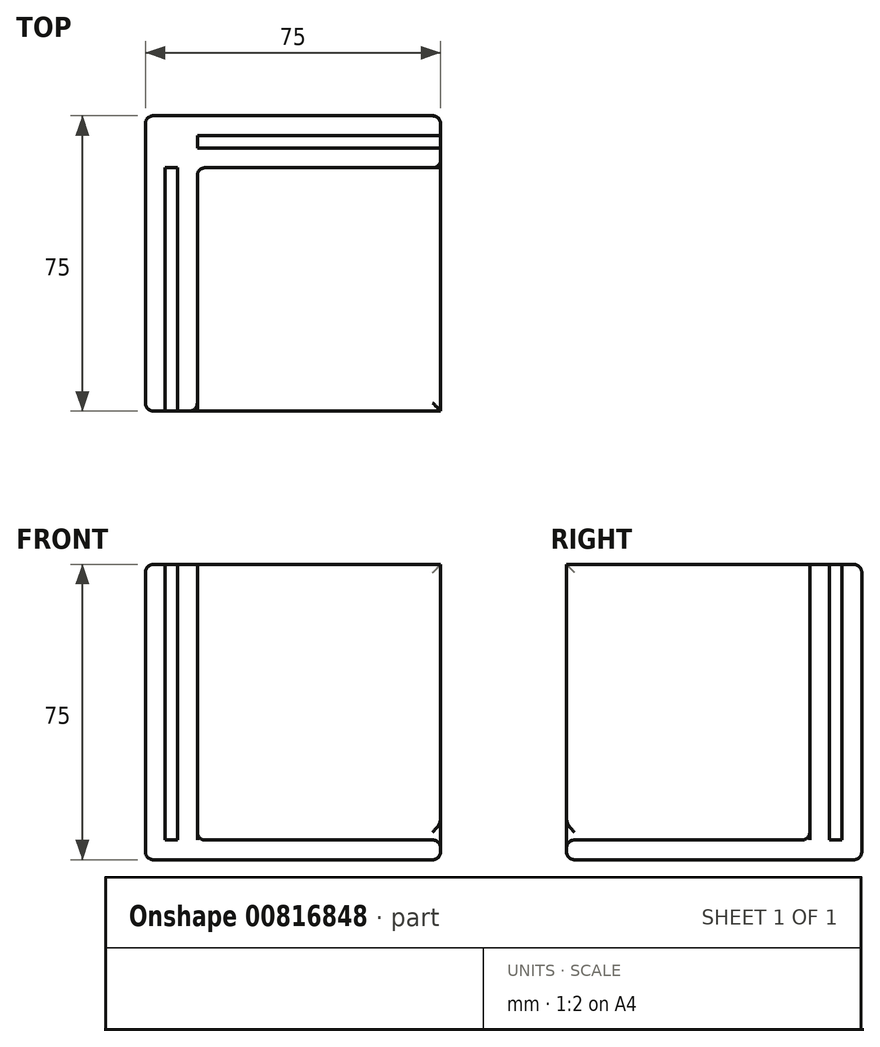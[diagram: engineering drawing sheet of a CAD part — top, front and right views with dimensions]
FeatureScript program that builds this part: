
annotation { "Feature Type Name" : "Feature", "Feature Type Description" : "" }
export const myFeature = defineFeature(function(context is Context, id is Id, definition is map)
    precondition{}
    {
        {
            var Q0;
            Q0=qCreatedBy(makeId("Top.planeOp"),FACE);
            var sketch = newSketch(context, id + "F0", { "sketchPlane" : qUnion([Q0])});
            skLineSegment(sketch, "E0.bottom", {"start": v(37.5, -37.5) * mm, "end": v(-37.5, -37.5) * mm});
            skLineSegment(sketch, "E0.top", {"start": v(37.5, 37.5) * mm, "end": v(-37.5, 37.5) * mm});
            skLineSegment(sketch, "E0.left", {"start": v(37.5, -37.5) * mm, "end": v(37.5, 37.5) * mm});
            skLineSegment(sketch, "E0.right", {"start": v(-37.5, -37.5) * mm, "end": v(-37.5, 37.5) * mm});
            skPoint(sketch, "E0.middle", {"position": v(0, 0) * mm});
            skSolve(sketch);
        }
        {
            var Q0;
            Q0=qSketchRegion(id+"F0",true);
            extrude(context, id + "F1", {"entities" : qUnion([Q0]), "depth" : 5 * mm, "offsetDistance" : 25 * mm});
        }
        {
            var Q0;
            Q0=makeQuery(id+"F1.opExtrude","CAP_FACE",FACE,{"disambiguationData":[OSD([sQuery(id+"F0.wireOp",EDGE,"E0.bottom"),sQuery(id+"F0.wireOp",EDGE,"E0.top"),sQuery(id+"F0.wireOp",EDGE,"E0.left"),sQuery(id+"F0.wireOp",EDGE,"E0.right")])],"isStart":false});
            var sketch = newSketch(context, id + "F2", { "sketchPlane" : qUnion([Q0])});
            skLineSegment(sketch, "E1.bottom", {"start": v(-37.5, 37.5) * mm, "end": v(-32.5, 37.5) * mm});
            skLineSegment(sketch, "E1.top", {"start": v(-37.5, -37.5) * mm, "end": v(-32.5, -37.5) * mm});
            skLineSegment(sketch, "E1.left", {"start": v(-37.5, 37.5) * mm, "end": v(-37.5, -37.5) * mm});
            skLineSegment(sketch, "E1.right", {"start": v(-32.5, 37.5) * mm, "end": v(-32.5, -37.5) * mm});
            skLineSegment(sketch, "E2.bottom", {"start": v(37.5, 37.5) * mm, "end": v(-37.5, 37.5) * mm});
            skLineSegment(sketch, "E2.top", {"start": v(37.5, 32.5) * mm, "end": v(-37.5, 32.5) * mm});
            skLineSegment(sketch, "E2.left", {"start": v(37.5, 37.5) * mm, "end": v(37.5, 32.5) * mm});
            skLineSegment(sketch, "E2.right", {"start": v(-37.5, 37.5) * mm, "end": v(-37.5, 32.5) * mm});
            skLineSegment(sketch, "E3.bottom", {"start": v(-29.3, 37.5) * mm, "end": v(-24.3, 37.5) * mm});
            skLineSegment(sketch, "E3.top", {"start": v(-29.3, -37.5) * mm, "end": v(-24.3, -37.5) * mm});
            skLineSegment(sketch, "E3.left", {"start": v(-29.3, 37.5) * mm, "end": v(-29.3, -37.5) * mm});
            skLineSegment(sketch, "E3.right", {"start": v(-24.3, 37.5) * mm, "end": v(-24.3, -37.5) * mm});
            skLineSegment(sketch, "E4.bottom", {"start": v(-37.5, 29.3) * mm, "end": v(37.5, 29.3) * mm});
            skLineSegment(sketch, "E4.top", {"start": v(-37.5, 24.3) * mm, "end": v(37.5, 24.3) * mm});
            skLineSegment(sketch, "E4.left", {"start": v(-37.5, 29.3) * mm, "end": v(-37.5, 24.3) * mm});
            skLineSegment(sketch, "E4.right", {"start": v(37.5, 29.3) * mm, "end": v(37.5, 24.3) * mm});
            skSolve(sketch);
        }
        {
            var Q0;
            Q0=qSketchRegion(id+"F2",true);
            extrude(context, id + "F3", {"entities" : qUnion([Q0]), "operationType" : NewBodyOperationType.ADD, "depth" : 70 * mm, "offsetDistance" : 25 * mm});
        }
        {
            var Q0;
            Q0=makeQuery(id+"F1.opExtrude","CAP_FACE",FACE,{"disambiguationData":[OSD([sQuery(id+"F0.wireOp",EDGE,"E0.bottom"),sQuery(id+"F0.wireOp",EDGE,"E0.top"),sQuery(id+"F0.wireOp",EDGE,"E0.left"),sQuery(id+"F0.wireOp",EDGE,"E0.right")])],"isStart":true});
            var Q1;
            Q1=makeQuery(id+"F3.boolean.opBoolean","MERGE",FACE,{"derivedFrom":[makeQuery(id+"F1.opExtrude","SWEPT_FACE",FACE,{"disambiguationData":[OSD([sQuery(id+"F0.wireOp",EDGE,"E0.right")])]}),makeQuery(id+"F3.opExtrude","SWEPT_FACE",FACE,{"disambiguationData":[OSD([sQuery(id+"F2.wireOp",EDGE,"M5YcsCfr-pvcU-yWks-6ihz-tbSOXkpsQLRh.left")])]})]});
            var Q2;
            Q2=makeQuery(id+"F3.boolean.opBoolean","MERGE",FACE,{"derivedFrom":[makeQuery(id+"F1.opExtrude","SWEPT_FACE",FACE,{"disambiguationData":[OSD([sQuery(id+"F0.wireOp",EDGE,"E0.top")])]}),makeQuery(id+"F3.opExtrude","SWEPT_FACE",FACE,{"disambiguationData":[OSD([sQuery(id+"F2.wireOp",EDGE,"M5YcsCfr-pvcU-yWks-6ihz-tbSOXkpsQLRh.top"),sQuery(id+"F2.wireOp",EDGE,"3u02SwK4-xcQg-xW4M-OONb-UyZOXjzJWRte.top")])]})]});
            var Q3;
            {var subQ0=sQuery(id+"F0.wireOp",EDGE,"E0.left");var subQ1=sQuery(id+"F0.wireOp",EDGE,"E0.bottom");Q3=makeQuery(id+"F3.boolean.opBoolean","SPLIT",FACE,{"disambiguationData":[TD([makeQuery(id+"F3.opExtrude","SWEPT_FACE",FACE,{"disambiguationData":[OSD([sQuery(id+"F2.wireOp",EDGE,"U4OE86xM-2nj9-5kqX-hZhN-euJrliqOmqsM.right")])]})])],"derivedFrom":makeQuery(id+"F1.opExtrude","CAP_FACE",FACE,{"disambiguationData":[OSD([subQ1,sQuery(id+"F0.wireOp",EDGE,"E0.top"),subQ0,sQuery(id+"F0.wireOp",EDGE,"E0.right")])],"isStart":false})});}
            var Q4;
            Q4=makeQuery(id+"F3.opExtrude","SWEPT_EDGE",EDGE,{"disambiguationData":[OSD([sQuery(id+"F2.wireOp",EDGE,"U4OE86xM-2nj9-5kqX-hZhN-euJrliqOmqsM.right"),sQuery(id+"F2.wireOp",EDGE,"hKQ6JI1m-YdC8-uINN-MBrZ-ORUy9FCE7vJ7.top"),sQuery(id+"F2.wireOp",EDGE,"hKQ6JI1m-YdC8-uINN-MBrZ-ORUy9FCE7vJ7.left")])]});
            var Q5;
            Q5=makeQuery(id+"F3.opExtrude","SWEPT_EDGE",EDGE,{"disambiguationData":[OSD([sQuery(id+"F2.wireOp",EDGE,"E3.right"),sQuery(id+"F2.wireOp",EDGE,"E4.top")])]});
            var Q6;
            {var subQ0=sQuery(id+"F2.wireOp",EDGE,"E4.top");Q6=makeQuery(id+"F3.opExtrude","CAP_EDGE",EDGE,{"disambiguationData":[OSD([subQ0]),TDD([makeQuery(id+"F2.imprint","IMPRINT",EDGE,{"disambiguationData":[TD([[makeQuery(id+"F2.imprint","INTERSECT",VERTEX,{"derivedFrom":[sQuery(id+"F2.wireOp",EDGE,"E3.right"),subQ0]}),-1.0]])],"derivedFrom":subQ0})])],"isStart":true});}
            var Q7;
            {var subQ0=sQuery(id+"F2.wireOp",EDGE,"E3.right");Q7=makeQuery(id+"F3.opExtrude","CAP_EDGE",EDGE,{"disambiguationData":[OSD([subQ0]),TDD([makeQuery(id+"F2.imprint","IMPRINT",EDGE,{"disambiguationData":[TD([[makeQuery(id+"F2.imprint","INTERSECT",VERTEX,{"derivedFrom":[subQ0,sQuery(id+"F2.wireOp",EDGE,"E4.top")]}),-1.0]])],"derivedFrom":subQ0})])],"isStart":true});}
            var Q8;
            {var subQ0=sQuery(id+"F0.wireOp",EDGE,"E0.left");var subQ1=sQuery(id+"F2.wireOp",EDGE,"E3.right");var subQ3=sQuery(id+"F0.wireOp",EDGE,"E0.bottom");var subQ4=sQuery(id+"F2.wireOp",EDGE,"E4.top");var subQ5=makeQuery(id+"F2.imprint","INTERSECT",VERTEX,{"derivedFrom":[subQ1,subQ4]});Q8=makeQuery(id+"F3.boolean.opBoolean","SPLIT",FACE,{"disambiguationData":[TD([makeQuery(id+"F3.opExtrude","SWEPT_FACE",FACE,{"disambiguationData":[OSD([subQ1]),TDD([makeQuery(id+"F2.imprint","IMPRINT",EDGE,{"disambiguationData":[TD([[subQ5,-1.0]])],"derivedFrom":subQ1})])]})])],"derivedFrom":makeQuery(id+"F1.opExtrude","CAP_FACE",FACE,{"disambiguationData":[OSD([subQ3,sQuery(id+"F0.wireOp",EDGE,"E0.top"),subQ0,sQuery(id+"F0.wireOp",EDGE,"E0.right")])],"isStart":false})});}
            fillet(context, id + "F4", {"entities" : qUnion([Q0, Q1, Q2, Q3, Q4, Q5, Q6, Q7, Q8]), "radius" : 2 * mm, "tangentPropagation" : true, "allowEdgeOverflow" : false});
        }
        {
            var Q0;
            Q0=makeQuery(id+"F3.opExtrude","CAP_FACE",FACE,{"disambiguationData":[OSD([sQuery(id+"F2.wireOp",EDGE,"E1.top"),sQuery(id+"F2.wireOp",EDGE,"E1.left"),sQuery(id+"F2.wireOp",EDGE,"E1.right"),sQuery(id+"F2.wireOp",EDGE,"E2.bottom"),sQuery(id+"F2.wireOp",EDGE,"E2.top"),sQuery(id+"F2.wireOp",EDGE,"E2.left"),sQuery(id+"F2.wireOp",EDGE,"E2.right"),sQuery(id+"F2.wireOp",EDGE,"E3.bottom"),sQuery(id+"F2.wireOp",EDGE,"E3.top"),sQuery(id+"F2.wireOp",EDGE,"E3.left"),sQuery(id+"F2.wireOp",EDGE,"E3.right"),sQuery(id+"F2.wireOp",EDGE,"E4.bottom"),sQuery(id+"F2.wireOp",EDGE,"E4.top"),sQuery(id+"F2.wireOp",EDGE,"E4.left"),sQuery(id+"F2.wireOp",EDGE,"E4.right")])],"isStart":false});
            var sketch = newSketch(context, id + "F5", { "sketchPlane" : qUnion([Q0])});
            skLineSegment(sketch, "E5.bottom", {"start": v(-32.5, 32.5) * mm, "end": v(-29.3, 32.5) * mm});
            skLineSegment(sketch, "E5.top", {"start": v(-32.5, 29.3) * mm, "end": v(-29.3, 29.3) * mm});
            skLineSegment(sketch, "E5.left", {"start": v(-32.5, 32.5) * mm, "end": v(-32.5, 29.3) * mm});
            skLineSegment(sketch, "E5.right", {"start": v(-29.3, 32.5) * mm, "end": v(-29.3, 29.3) * mm});
            skSolve(sketch);
        }
        {
            var Q0;
            Q0=qSketchRegion(id+"F5",true);
            var Q1;
            Q1=makeQuery(id+"F1.opExtrude","CAP_FACE",FACE,{"disambiguationData":[OSD([sQuery(id+"F0.wireOp",EDGE,"E0.bottom"),sQuery(id+"F0.wireOp",EDGE,"E0.top"),sQuery(id+"F0.wireOp",EDGE,"E0.left"),sQuery(id+"F0.wireOp",EDGE,"E0.right")])],"isStart":true});
            extrude(context, id + "F6", {"entities" : qUnion([Q0]), "operationType" : NewBodyOperationType.ADD, "endBound" : BoundingType.UP_TO_SURFACE, "oppositeDirection" : true, "depth" : 25 * mm, "endBoundEntityFace" : qUnion([Q1]), "offsetDistance" : 25 * mm});
        }
    });
